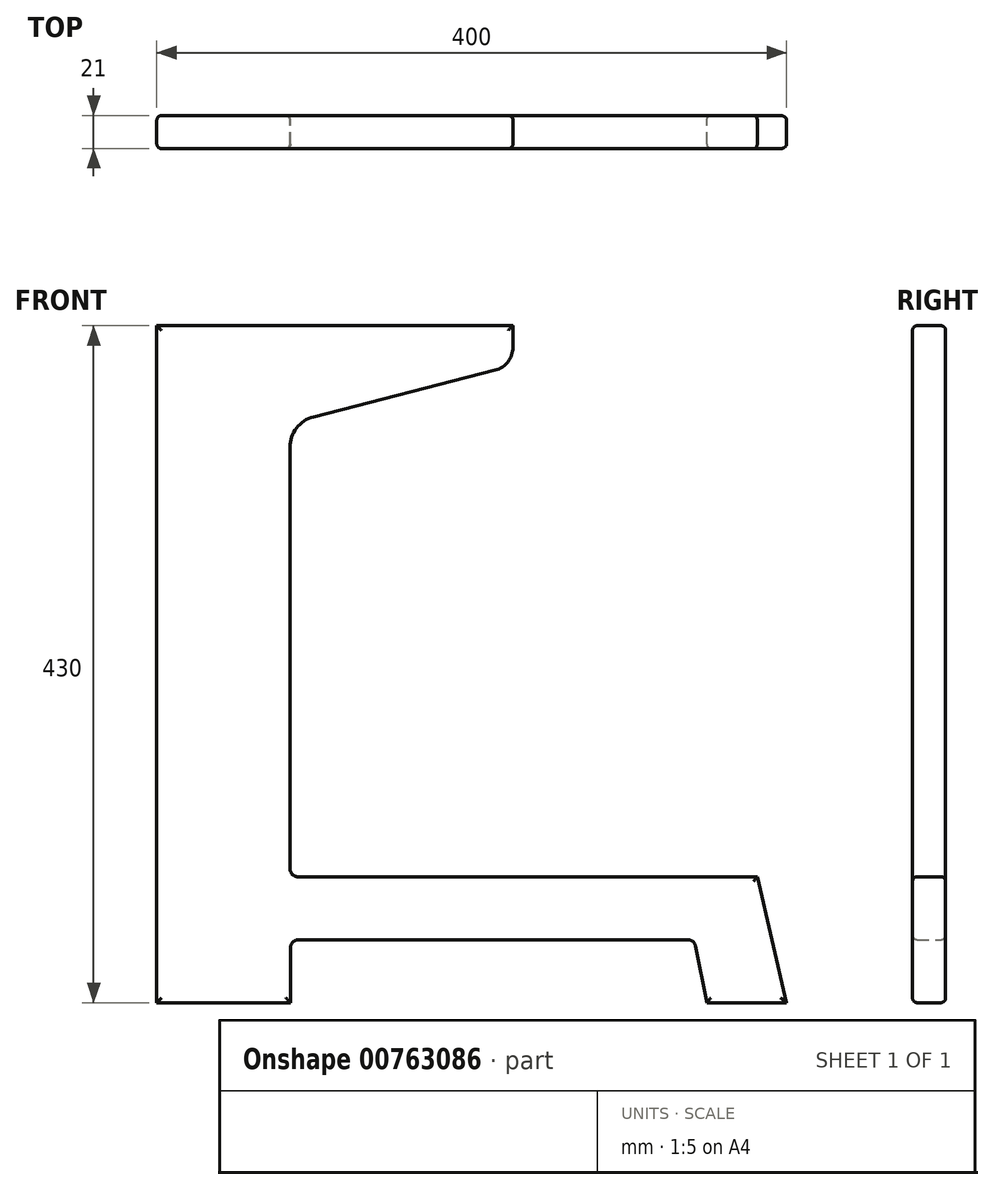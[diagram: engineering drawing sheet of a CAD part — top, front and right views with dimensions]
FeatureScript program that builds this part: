
annotation { "Feature Type Name" : "Feature", "Feature Type Description" : "" }
export const myFeature = defineFeature(function(context is Context, id is Id, definition is map)
    precondition{}
    {
        {
            var Q0;
            Q0=qCreatedBy(makeId("Front.planeOp"),FACE);
            var sketch = newSketch(context, id + "F0", { "sketchPlane" : qUnion([Q0])});
            skLineSegment(sketch, "E0", {"start": v(0, 0) * mm, "end": v(0, 450) * mm, "construction": true});
            skLineSegment(sketch, "E1", {"start": v(0, 0) * mm, "end": v(400, 0) * mm, "construction": true});
            skLineSegment(sketch, "E2", {"start": v(400, 0) * mm, "end": v(400, 80) * mm, "construction": true});
            skLineSegment(sketch, "E3", {"start": v(400, 80) * mm, "end": v(89.6, 80) * mm, "construction": true});
            skLineSegment(sketch, "E4", {"start": v(400, 80) * mm, "end": v(400, 100) * mm, "construction": true});
            skLineSegment(sketch, "E5", {"start": v(400, 100) * mm, "end": v(0, 100) * mm, "construction": true});
            skLineSegment(sketch, "E6", {"start": v(381.4, 80) * mm, "end": v(400, 0) * mm});
            skLineSegment(sketch, "E7", {"start": v(0, 0) * mm, "end": v(0, 430) * mm});
            skLineSegment(sketch, "E8", {"start": v(0, 430) * mm, "end": v(226.23, 430) * mm});
            skLineSegment(sketch, "E9", {"start": v(84.6, 352.7) * mm, "end": v(84.6, 85) * mm});
            skLineSegment(sketch, "E10", {"start": v(85, 35) * mm, "end": v(85, 0) * mm});
            skLineSegment(sketch, "E11", {"start": v(90, 40) * mm, "end": v(337.26, 40) * mm});
            skLineSegment(sketch, "E12", {"start": v(400, 0) * mm, "end": v(349.36, 0) * mm});
            skLineSegment(sketch, "E13", {"start": v(349.36, 0) * mm, "end": v(342.16, 35.98) * mm});
            skLineSegment(sketch, "E14", {"start": v(0, 0) * mm, "end": v(85, 0) * mm});
            skArc(sketch, "E15.filletArc", {"start": v(342.16, 35.98) * mm, "mid": v(340.43, 38.87) * mm, "end": v(337.26, 40) * mm});
            skPoint(sketch, "E16.newPointA", {"position": v(85, 80) * mm});
            skPoint(sketch, "E16.newPointB", {"position": v(85, 40) * mm});
            skArc(sketch, "E16.filletArc", {"start": v(90, 40) * mm, "mid": v(86.46, 38.54) * mm, "end": v(85, 35) * mm});
            skPoint(sketch, "E17.newPointB", {"position": v(0, 80) * mm});
            skArc(sketch, "E17.filletArc", {"start": v(84.6, 85) * mm, "mid": v(86.06, 81.46) * mm, "end": v(89.6, 80) * mm});
            skLineSegment(sketch, "E18", {"start": v(89.6, 80) * mm, "end": v(381.4, 80) * mm});
            skLineSegment(sketch, "E19", {"start": v(226.23, 430) * mm, "end": v(226.23, 416.25) * mm});
            skLineSegment(sketch, "E20", {"start": v(214.97, 401.72) * mm, "end": v(99.62, 372.08) * mm});
            skArc(sketch, "E21.filletArc", {"start": v(99.62, 372.08) * mm, "mid": v(88.8, 364.96) * mm, "end": v(84.6, 352.7) * mm});
            skPoint(sketch, "E22.visualSharp", {"position": v(226.23, 404.62) * mm});
            skArc(sketch, "E22.filletArc", {"start": v(214.97, 401.72) * mm, "mid": v(223.09, 407.06) * mm, "end": v(226.23, 416.25) * mm});
            skSolve(sketch);
        }
        {
            var Q0;
            Q0=makeQuery(id+"F0.imprint","IMPRINT",FACE,{"disambiguationData":[TD([[makeQuery(id+"F0.imprint","IMPRINT",EDGE,{"derivedFrom":sQuery(id+"F0.wireOp",EDGE,"E7")}),-1.0]])]});
            extrude(context, id + "F1", {"entities" : qUnion([Q0]), "depth" : 21 * mm, "offsetDistance" : 25 * mm});
        }
        {
            var Q0;
            Q0=makeQuery(id+"F1.opExtrude","CAP_FACE",FACE,{"disambiguationData":[OSD([sQuery(id+"F0.wireOp",EDGE,"E6"),sQuery(id+"F0.wireOp",EDGE,"E7"),sQuery(id+"F0.wireOp",EDGE,"E8"),sQuery(id+"F0.wireOp",EDGE,"hpRhQfVd-IyYa-hwGC-31Pa-SSjwoI7HafpN"),sQuery(id+"F0.wireOp",EDGE,"2anZZDai-CEc6-KzzX-dAyT-y1rN5zEr7RGD"),sQuery(id+"F0.wireOp",EDGE,"E9"),sQuery(id+"F0.wireOp",EDGE,"E10"),sQuery(id+"F0.wireOp",EDGE,"E11"),sQuery(id+"F0.wireOp",EDGE,"E12"),sQuery(id+"F0.wireOp",EDGE,"E13"),sQuery(id+"F0.wireOp",EDGE,"E14"),sQuery(id+"F0.wireOp",EDGE,"3a7b9edf-ba22-4f8d-a28f-f8634016295e.filletArc"),sQuery(id+"F0.wireOp",EDGE,"8a8ece1f-a573-40ab-a9e9-4ea46d882f8e.filletArc"),sQuery(id+"F0.wireOp",EDGE,"E15.filletArc"),sQuery(id+"F0.wireOp",EDGE,"E16.filletArc"),sQuery(id+"F0.wireOp",EDGE,"E17.filletArc"),sQuery(id+"F0.wireOp",EDGE,"E18")])],"isStart":false});
            var Q1;
            Q1=makeQuery(id+"F1.opExtrude","CAP_FACE",FACE,{"disambiguationData":[OSD([sQuery(id+"F0.wireOp",EDGE,"E6"),sQuery(id+"F0.wireOp",EDGE,"E7"),sQuery(id+"F0.wireOp",EDGE,"E8"),sQuery(id+"F0.wireOp",EDGE,"hpRhQfVd-IyYa-hwGC-31Pa-SSjwoI7HafpN"),sQuery(id+"F0.wireOp",EDGE,"2anZZDai-CEc6-KzzX-dAyT-y1rN5zEr7RGD"),sQuery(id+"F0.wireOp",EDGE,"E9"),sQuery(id+"F0.wireOp",EDGE,"E10"),sQuery(id+"F0.wireOp",EDGE,"E11"),sQuery(id+"F0.wireOp",EDGE,"E12"),sQuery(id+"F0.wireOp",EDGE,"E13"),sQuery(id+"F0.wireOp",EDGE,"E14"),sQuery(id+"F0.wireOp",EDGE,"3a7b9edf-ba22-4f8d-a28f-f8634016295e.filletArc"),sQuery(id+"F0.wireOp",EDGE,"8a8ece1f-a573-40ab-a9e9-4ea46d882f8e.filletArc"),sQuery(id+"F0.wireOp",EDGE,"E15.filletArc"),sQuery(id+"F0.wireOp",EDGE,"E16.filletArc"),sQuery(id+"F0.wireOp",EDGE,"E17.filletArc"),sQuery(id+"F0.wireOp",EDGE,"E18")])],"isStart":true});
            fillet(context, id + "F2", {"entities" : qUnion([Q0, Q1]), "radius" : 3 * mm, "tangentPropagation" : true, "allowEdgeOverflow" : false});
        }
        {
            var Q0;
            Q0=makeQuery(id+"F1.opExtrude","CAP_FACE",FACE,{"disambiguationData":[OSD([sQuery(id+"F0.wireOp",EDGE,"E6"),sQuery(id+"F0.wireOp",EDGE,"E7"),sQuery(id+"F0.wireOp",EDGE,"E8"),sQuery(id+"F0.wireOp",EDGE,"hpRhQfVd-IyYa-hwGC-31Pa-SSjwoI7HafpN"),sQuery(id+"F0.wireOp",EDGE,"2anZZDai-CEc6-KzzX-dAyT-y1rN5zEr7RGD"),sQuery(id+"F0.wireOp",EDGE,"E9"),sQuery(id+"F0.wireOp",EDGE,"E10"),sQuery(id+"F0.wireOp",EDGE,"E11"),sQuery(id+"F0.wireOp",EDGE,"E12"),sQuery(id+"F0.wireOp",EDGE,"E13"),sQuery(id+"F0.wireOp",EDGE,"E14"),sQuery(id+"F0.wireOp",EDGE,"3a7b9edf-ba22-4f8d-a28f-f8634016295e.filletArc"),sQuery(id+"F0.wireOp",EDGE,"8a8ece1f-a573-40ab-a9e9-4ea46d882f8e.filletArc"),sQuery(id+"F0.wireOp",EDGE,"E15.filletArc"),sQuery(id+"F0.wireOp",EDGE,"E16.filletArc"),sQuery(id+"F0.wireOp",EDGE,"E17.filletArc"),sQuery(id+"F0.wireOp",EDGE,"E18")])],"isStart":false});
            var sketch = newSketch(context, id + "F3", { "sketchPlane" : qUnion([Q0])});
            skLineSegment(sketch, "E23", {"start": v(3, 62.47) * mm, "end": v(103, 62.47) * mm, "construction": true});
            skSolve(sketch);
        }
        {
            var Q0;
            Q0=makeQuery(id+"F1.opExtrude","CAP_FACE",FACE,{"disambiguationData":[OSD([sQuery(id+"F0.wireOp",EDGE,"E6"),sQuery(id+"F0.wireOp",EDGE,"E7"),sQuery(id+"F0.wireOp",EDGE,"E8"),sQuery(id+"F0.wireOp",EDGE,"hpRhQfVd-IyYa-hwGC-31Pa-SSjwoI7HafpN"),sQuery(id+"F0.wireOp",EDGE,"2anZZDai-CEc6-KzzX-dAyT-y1rN5zEr7RGD"),sQuery(id+"F0.wireOp",EDGE,"E9"),sQuery(id+"F0.wireOp",EDGE,"E10"),sQuery(id+"F0.wireOp",EDGE,"E11"),sQuery(id+"F0.wireOp",EDGE,"E12"),sQuery(id+"F0.wireOp",EDGE,"E13"),sQuery(id+"F0.wireOp",EDGE,"E14"),sQuery(id+"F0.wireOp",EDGE,"3a7b9edf-ba22-4f8d-a28f-f8634016295e.filletArc"),sQuery(id+"F0.wireOp",EDGE,"8a8ece1f-a573-40ab-a9e9-4ea46d882f8e.filletArc"),sQuery(id+"F0.wireOp",EDGE,"E15.filletArc"),sQuery(id+"F0.wireOp",EDGE,"E16.filletArc"),sQuery(id+"F0.wireOp",EDGE,"E17.filletArc"),sQuery(id+"F0.wireOp",EDGE,"E18")])],"isStart":true});
            var sketch = newSketch(context, id + "F4", { "sketchPlane" : qUnion([Q0])});
            skLineSegment(sketch, "E24", {"start": v(-3, 62.42) * mm, "end": v(-103, 62.42) * mm, "construction": true});
            skSolve(sketch);
        }
        {
            var Q0;
            Q0=makeQuery(id+"F1.opExtrude","SWEPT_FACE",FACE,{"disambiguationData":[OSD([sQuery(id+"F0.wireOp",EDGE,"E18")])]});
            var sketch = newSketch(context, id + "F5", { "sketchPlane" : qUnion([Q0])});
            skLineSegment(sketch, "E25", {"start": v(89.6, -10.5) * mm, "end": v(171.6, -10.5) * mm});
            skSolve(sketch);
        }
        {
            var Q0;
            Q0=makeQuery(id+"F1.opExtrude","SWEPT_FACE",FACE,{"disambiguationData":[OSD([sQuery(id+"F0.wireOp",EDGE,"E8")])]});
            var sketch = newSketch(context, id + "F6", { "sketchPlane" : qUnion([Q0])});
            skLineSegment(sketch, "E26", {"start": v(0, -10.5) * mm, "end": v(82, -10.5) * mm});
            skSolve(sketch);
        }
    });
